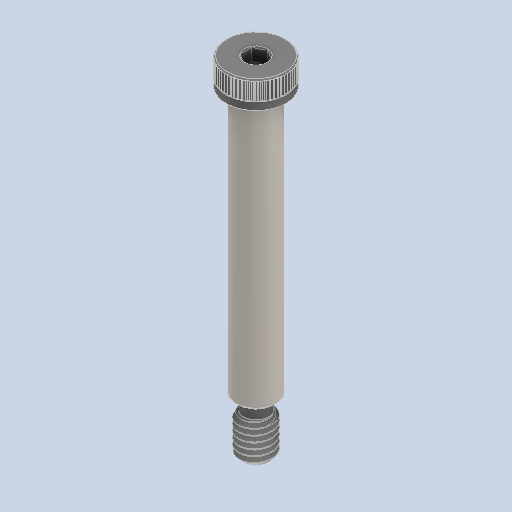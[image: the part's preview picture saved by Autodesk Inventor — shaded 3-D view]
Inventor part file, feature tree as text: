
AUTODESK INVENTOR PART (.ipt)
format: ipt  version: 2024.2 (Build 282272000, 272)  size: 428,032 bytes
history: native  units: in
note: dims shown in document units (in); Inventor stores cm internally (conversion verified against a paired STEP export)
features: chamfer x1
ambient origin geometry x8: Origin, YZ Plane, XZ Plane, XY Plane, X Axis, Y Axis, Z Axis, Center Point
bodies: Solid1 (feature_tree)
feature tree (1):
  chamfer  "Chamfer3"  [1 undecoded]
note: 1 required parameter value undecoded (feature->parameter linkage not recoverable at this tier; creation-order binding heuristic only, values carry confidence <= 0.55)
